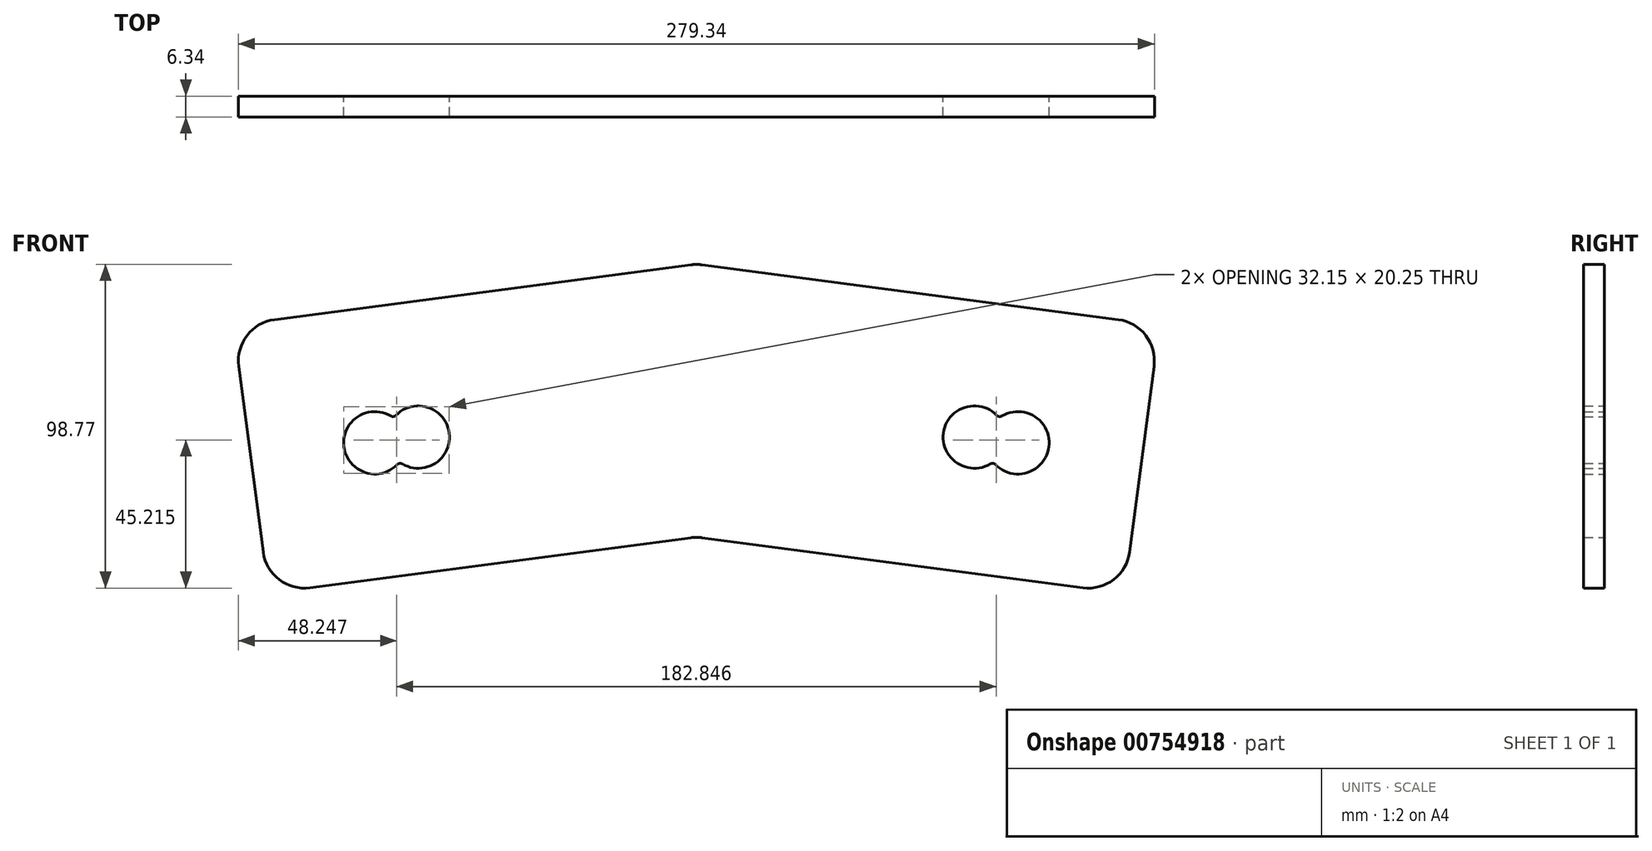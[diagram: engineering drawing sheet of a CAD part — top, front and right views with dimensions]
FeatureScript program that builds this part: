
annotation { "Feature Type Name" : "Feature", "Feature Type Description" : "" }
export const myFeature = defineFeature(function(context is Context, id is Id, definition is map)
    precondition{}
    {
        {
            var Q0;
            Q0=qCreatedBy(makeId("Front.planeOp"),FACE);
            var sketch = newSketch(context, id + "F0", { "sketchPlane" : qUnion([Q0])});
            skLineSegment(sketch, "E0", {"start": v(0, 0) * mm, "end": v(-130.44, -17.17) * mm});
            skLineSegment(sketch, "E1", {"start": v(0, 0) * mm, "end": v(0, 83.26) * mm});
            skLineSegment(sketch, "E2", {"start": v(-130.44, -17.17) * mm, "end": v(-141.22, 64.67) * mm});
            skLineSegment(sketch, "E3", {"start": v(-141.22, 64.67) * mm, "end": v(0, 83.26) * mm});
            skPoint(sketch, "E4", {"position": v(-15.88, 90.78) * mm});
            skPoint(sketch, "E5", {"position": v(-15.88, -11.7) * mm});
            skLineSegment(sketch, "E6.MirrorCS", {"start": v(0, 0) * mm, "end": v(130.44, -17.17) * mm});
            skPoint(sketch, "E7.MirrorP", {"position": v(15.88, -11.7) * mm});
            skLineSegment(sketch, "E8.MirrorCS", {"start": v(130.44, -17.17) * mm, "end": v(141.22, 64.67) * mm});
            skLineSegment(sketch, "E9.MirrorCS", {"start": v(141.22, 64.67) * mm, "end": v(0, 83.26) * mm});
            skPoint(sketch, "E10.MirrorP", {"position": v(15.88, 90.78) * mm});
            skLineSegment(sketch, "E11", {"start": v(-15.88, -11.7) * mm, "end": v(-25.82, 63.85) * mm, "construction": true});
            skLineSegment(sketch, "E12", {"start": v(-15.88, 90.78) * mm, "end": v(-5.93, 15.23) * mm, "construction": true});
            skLineSegment(sketch, "E13", {"start": v(-103.44, 69.64) * mm, "end": v(-92.67, -12.2) * mm, "construction": true});
            skPoint(sketch, "E14", {"position": v(-98.05, 28.72) * mm});
            skLineSegment(sketch, "E15", {"start": v(-98.05, 28.72) * mm, "end": v(-22.5, 38.67) * mm, "construction": true});
            skCircle(sketch, "E16", {"center": v(-98.05, 28.72) * mm, "radius": 9.53 * mm});
            skLineSegment(sketch, "E17", {"start": v(-90.18, 71.39) * mm, "end": v(-79.4, -10.45) * mm, "construction": true});
            skLineSegment(sketch, "E18", {"start": v(-79.4, -10.45) * mm, "end": v(-84.8, 30.47) * mm});
            skLineSegment(sketch, "E19", {"start": v(-84.8, 30.47) * mm, "end": v(-9.24, 40.41) * mm, "construction": true});
            skCircle(sketch, "E20", {"center": v(-84.8, 30.47) * mm, "radius": 9.53 * mm});
            skCircle(sketch, "E21.MirrorC", {"center": v(84.8, 30.47) * mm, "radius": 9.53 * mm});
            skCircle(sketch, "E22.MirrorC", {"center": v(98.05, 28.72) * mm, "radius": 9.53 * mm});
            skLineSegment(sketch, "E23", {"start": v(-135.83, 23.75) * mm, "end": v(-98.05, 28.72) * mm, "construction": true});
            skSolve(sketch);
        }
        {
            var Q0;
            Q0=qSketchRegion(id+"F0",true);
            extrude(context, id + "F1", {"entities" : qUnion([Q0]), "endBound" : BoundingType.SYMMETRIC, "depth" : 6.35 * mm, "offsetDistance" : 25.4 * mm});
        }
        {
            var Q0;
            Q0=makeQuery(id+"F1.opExtrude","SWEPT_EDGE",EDGE,{"disambiguationData":[OSD([sQuery(id+"F0.wireOp",EDGE,"E2"),sQuery(id+"F0.wireOp",EDGE,"E3")])]});
            var Q1;
            Q1=makeQuery(id+"F1.opExtrude","SWEPT_EDGE",EDGE,{"disambiguationData":[OSD([sQuery(id+"F0.wireOp",EDGE,"E3"),sQuery(id+"F0.wireOp",EDGE,"E1"),sQuery(id+"F0.wireOp",EDGE,"E9.MirrorCS")])]});
            var Q2;
            Q2=makeQuery(id+"F1.opExtrude","SWEPT_EDGE",EDGE,{"disambiguationData":[OSD([sQuery(id+"F0.wireOp",EDGE,"E0"),sQuery(id+"F0.wireOp",EDGE,"E6.MirrorCS"),sQuery(id+"F0.wireOp",EDGE,"E1")])]});
            var Q3;
            Q3=makeQuery(id+"F1.opExtrude","SWEPT_EDGE",EDGE,{"disambiguationData":[OSD([sQuery(id+"F0.wireOp",EDGE,"E6.MirrorCS"),sQuery(id+"F0.wireOp",EDGE,"E8.MirrorCS")])]});
            var Q4;
            Q4=makeQuery(id+"F1.opExtrude","SWEPT_EDGE",EDGE,{"disambiguationData":[OSD([sQuery(id+"F0.wireOp",EDGE,"E8.MirrorCS"),sQuery(id+"F0.wireOp",EDGE,"E9.MirrorCS")])]});
            var Q5;
            Q5=makeQuery(id+"F1.opExtrude","SWEPT_EDGE",EDGE,{"disambiguationData":[OSD([sQuery(id+"F0.wireOp",EDGE,"E0"),sQuery(id+"F0.wireOp",EDGE,"E2")])]});
            fillet(context, id + "F2", {"entities" : qUnion([Q0, Q1, Q2, Q3, Q4, Q5]), "radius" : 12.7 * mm, "tangentPropagation" : true, "allowEdgeOverflow" : false});
        }
        {
            var Q0;
            {var subQ0=sQuery(id+"F0.wireOp",EDGE,"E20");var subQ1=sQuery(id+"F0.wireOp",EDGE,"E16");Q0=makeQuery(id+"F1.opExtrude","SWEPT_EDGE",EDGE,{"disambiguationData":[OSD([subQ1,subQ0]),TDD([makeQuery(id+"F0.imprint","INTERSECT",VERTEX,{"disambiguationData":[OD(0.0)],"derivedFrom":[subQ1,subQ0]})])]});}
            var Q1;
            {var subQ0=sQuery(id+"F0.wireOp",EDGE,"E20");var subQ1=sQuery(id+"F0.wireOp",EDGE,"E16");Q1=makeQuery(id+"F1.opExtrude","SWEPT_EDGE",EDGE,{"disambiguationData":[OSD([subQ1,subQ0]),TDD([makeQuery(id+"F0.imprint","INTERSECT",VERTEX,{"disambiguationData":[OD(1.0)],"derivedFrom":[subQ1,subQ0]})])]});}
            fillet(context, id + "F3", {"entities" : qUnion([Q0, Q1]), "radius" : 1.27 * mm, "tangentPropagation" : true, "allowEdgeOverflow" : false});
        }
        {
            var Q0;
            {var subQ0=sQuery(id+"F0.wireOp",EDGE,"E22.MirrorC");var subQ1=sQuery(id+"F0.wireOp",EDGE,"E21.MirrorC");Q0=makeQuery(id+"F1.opExtrude","SWEPT_EDGE",EDGE,{"disambiguationData":[OSD([subQ1,subQ0]),TDD([makeQuery(id+"F0.imprint","INTERSECT",VERTEX,{"disambiguationData":[OD(0.0)],"derivedFrom":[subQ1,subQ0]})])]});}
            var Q1;
            {var subQ0=sQuery(id+"F0.wireOp",EDGE,"E22.MirrorC");var subQ1=sQuery(id+"F0.wireOp",EDGE,"E21.MirrorC");Q1=makeQuery(id+"F1.opExtrude","SWEPT_EDGE",EDGE,{"disambiguationData":[OSD([subQ1,subQ0]),TDD([makeQuery(id+"F0.imprint","INTERSECT",VERTEX,{"disambiguationData":[OD(1.0)],"derivedFrom":[subQ1,subQ0]})])]});}
            fillet(context, id + "F4", {"entities" : qUnion([Q0, Q1]), "radius" : 1.27 * mm, "tangentPropagation" : true, "allowEdgeOverflow" : false});
        }
    });
